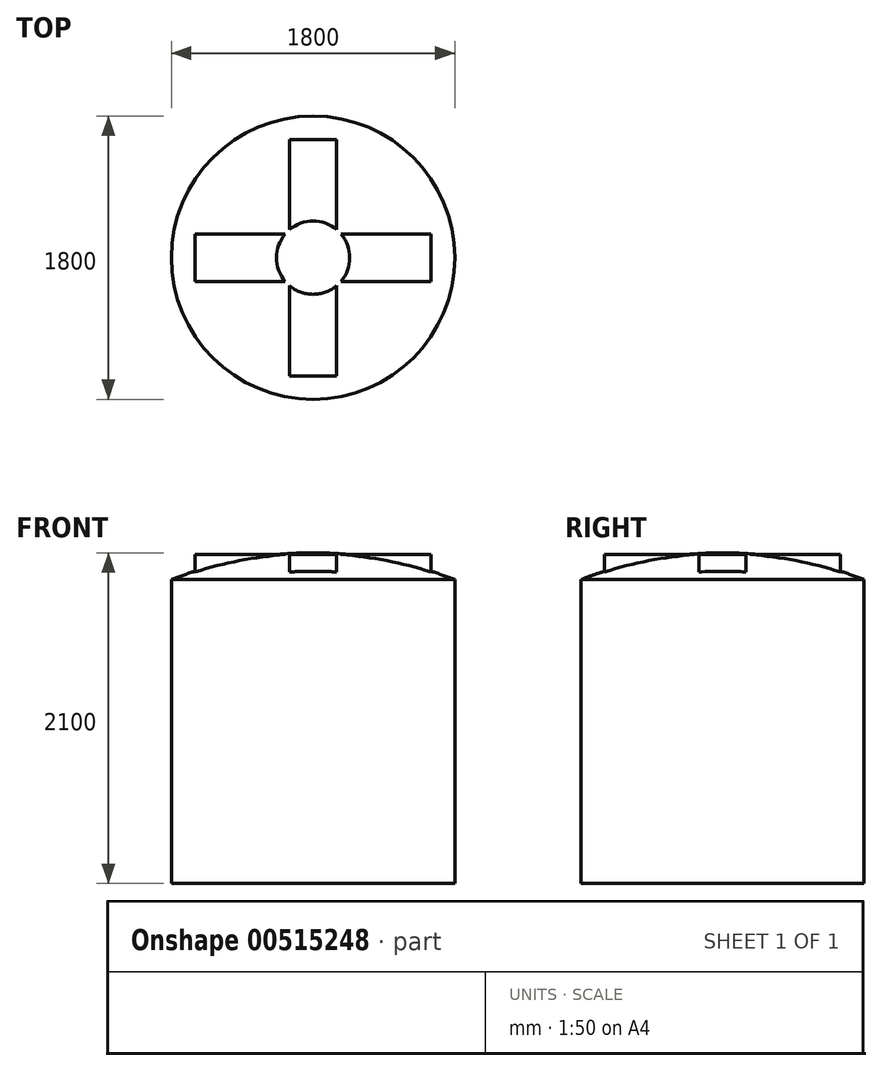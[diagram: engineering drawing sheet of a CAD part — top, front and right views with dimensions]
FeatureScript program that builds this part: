
annotation { "Feature Type Name" : "Feature", "Feature Type Description" : "" }
export const myFeature = defineFeature(function(context is Context, id is Id, definition is map)
    precondition{}
    {
        {
            var Q0;
            Q0=qCreatedBy(makeId("Top.planeOp"),FACE);
            cPlane(context, id + "F0", {"entities" : qUnion([Q0]), "cplaneType" : CPlaneType.OFFSET, "offset" : 1930 * mm, "width" : 150 * mm, "height" : 150 * mm});
        }
        {
            var Q0;
            Q0=qCreatedBy(makeId("Right.planeOp"),FACE);
            var sketch = newSketch(context, id + "F1", { "sketchPlane" : qUnion([Q0])});
            skLineSegment(sketch, "E0", {"start": v(0, 0) * mm, "end": v(-900, 0) * mm});
            skLineSegment(sketch, "E1", {"start": v(-900, 0) * mm, "end": v(-900, 1930) * mm});
            skArc(sketch, "E2", {"start": v(-900, 1930) * mm, "mid": v(-457.96, 2057.13) * mm, "end": v(0, 2100) * mm});
            skLineSegment(sketch, "E3", {"start": v(0, 2100) * mm, "end": v(0, 0) * mm});
            skLineSegment(sketch, "E4", {"start": v(0, 2100) * mm, "end": v(0, 3064.95) * mm, "construction": true});
            skSolve(sketch);
        }
        {
            var Q0;
            Q0=qCreatedBy(id+"F0.planeOp",FACE);
            var sketch = newSketch(context, id + "F2", { "sketchPlane" : qUnion([Q0])});
            skLineSegment(sketch, "E5.bottom", {"start": v(-150, 0) * mm, "end": v(150, 0) * mm});
            skLineSegment(sketch, "E5.top", {"start": v(-150, -750) * mm, "end": v(150, -750) * mm});
            skLineSegment(sketch, "E5.left", {"start": v(-150, 0) * mm, "end": v(-150, -750) * mm});
            skLineSegment(sketch, "E5.right", {"start": v(150, 0) * mm, "end": v(150, -750) * mm});
            skSolve(sketch);
        }
        {
            var Q0;
            Q0=makeQuery(id+"F1.imprint","IMPRINT",FACE,{"disambiguationData":[TD([[makeQuery(id+"F1.imprint","IMPRINT",EDGE,{"derivedFrom":sQuery(id+"F1.wireOp",EDGE,"E0")}),-1.0]])]});
            var Q1;
            Q1=sQuery(id+"F1.wireOp",EDGE,"E3");
            revolve(context, id + "F3", {"entities" : qUnion([Q0]), "axis" : qUnion([Q1]), "revolveType" : RevolveType.FULL});
        }
        {
            var Q0;
            Q0 = qSketchRegion(id + "F2", true);
            extrude(context, id + "F4", {"entities" : qUnion([Q0]), "depth" : 159 * mm, "offsetDistance" : 25 * mm});
        }
        {
            var Q0;
            Q0=makeQuery(id+"F4.opExtrude","SWEPT_BODY",BODY,{"disambiguationData":[OSD([sQuery(id+"F2.wireOp",EDGE,"E5.bottom"),sQuery(id+"F2.wireOp",EDGE,"E5.top"),sQuery(id+"F2.wireOp",EDGE,"E5.left"),sQuery(id+"F2.wireOp",EDGE,"E5.right")])]});
            var Q1;
            Q1=sQuery(id+"F1.wireOp",EDGE,"E4");
            circularPattern(context, id + "F5", {"operationType" : NewBodyOperationType.ADD, "entities" : qUnion([Q0]), "axis" : qUnion([Q1]), "angle" : 360 * degree, "instanceCount" : 4, "equalSpace" : true});
        }
    });
